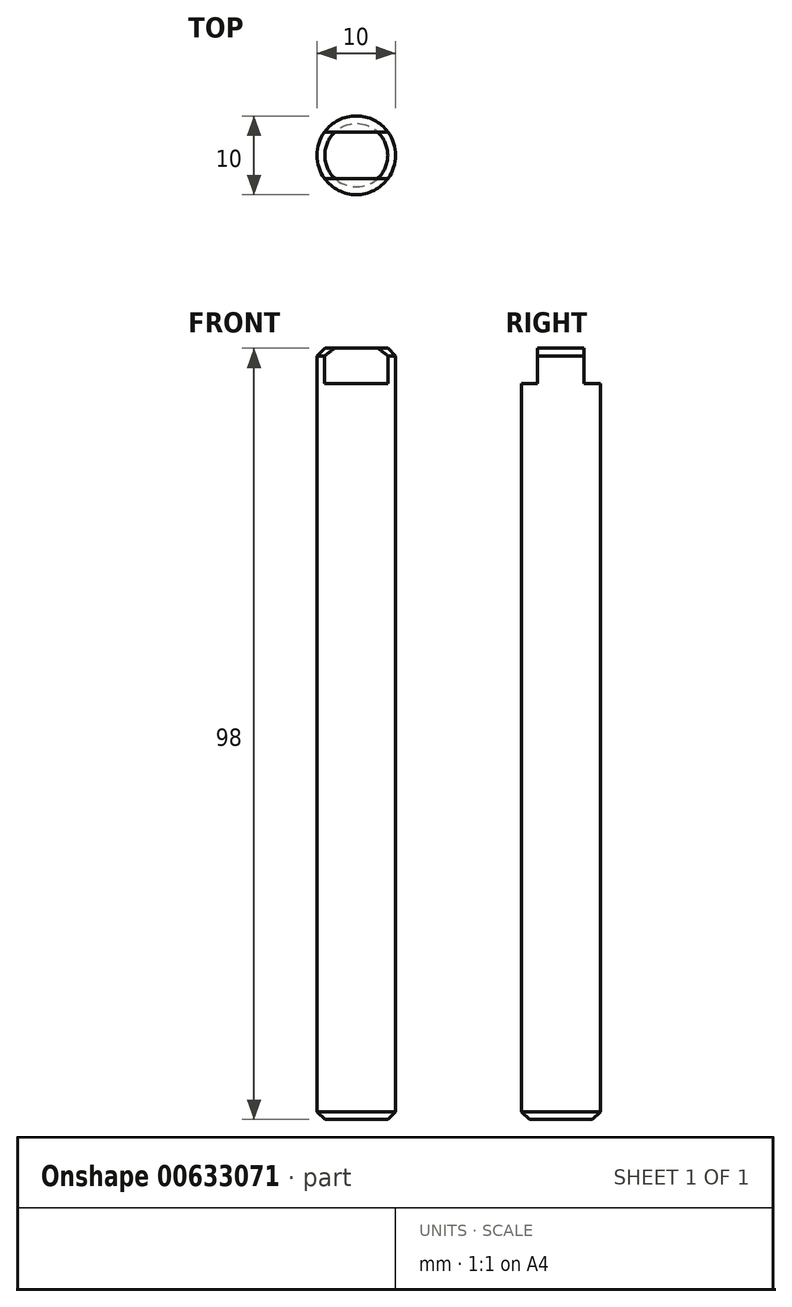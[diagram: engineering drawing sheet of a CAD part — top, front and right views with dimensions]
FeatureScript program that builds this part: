
annotation { "Feature Type Name" : "Feature", "Feature Type Description" : "" }
export const myFeature = defineFeature(function(context is Context, id is Id, definition is map)
    precondition{}
    {
        {
            var Q0;
            Q0=qCreatedBy(makeId("Top.planeOp"),FACE);
            var sketch = newSketch(context, id + "F0", { "sketchPlane" : qUnion([Q0])});
            skCircle(sketch, "E0", {"center": v(-1.1, 0) * mm, "radius": 5 * mm});
            skSolve(sketch);
        }
        {
            var Q0;
            Q0=makeQuery(id+"F0.imprint","IMPRINT",FACE,{"disambiguationData":[TD([[makeQuery(id+"F0.imprint","IMPRINT",EDGE,{"derivedFrom":sQuery(id+"F0.wireOp",EDGE,"E0")}),1.0]])]});
            extrude(context, id + "F1", {"entities" : qUnion([Q0]), "depth" : ((128.5 - 36.5) + 6) * mm, "offsetDistance" : 25 * mm});
        }
        {
            var Q0;
            Q0=qCreatedBy(makeId("Right.planeOp"),FACE);
            var sketch = newSketch(context, id + "F2", { "sketchPlane" : qUnion([Q0])});
            skLineSegment(sketch, "E1.bottom", {"start": v(2.95, 98) * mm, "end": v(7.82, 98) * mm});
            skLineSegment(sketch, "E1.top", {"start": v(2.95, 93.5) * mm, "end": v(7.82, 93.5) * mm});
            skLineSegment(sketch, "E1.left", {"start": v(2.95, 98) * mm, "end": v(2.95, 93.5) * mm});
            skLineSegment(sketch, "E1.right", {"start": v(7.82, 98) * mm, "end": v(7.82, 93.5) * mm});
            skLineSegment(sketch, "E2.bottom", {"start": v(-2.95, 98) * mm, "end": v(-8.14, 98) * mm});
            skLineSegment(sketch, "E2.top", {"start": v(-2.95, 93.5) * mm, "end": v(-8.14, 93.5) * mm});
            skLineSegment(sketch, "E2.left", {"start": v(-2.95, 98) * mm, "end": v(-2.95, 93.5) * mm});
            skLineSegment(sketch, "E2.right", {"start": v(-8.14, 98) * mm, "end": v(-8.14, 93.5) * mm});
            skSolve(sketch);
        }
        {
            var Q0;
            Q0 = qSketchRegion(id + "F2", true);
            extrude(context, id + "F3", {"entities" : qUnion([Q0]), "operationType" : NewBodyOperationType.REMOVE, "endBound" : BoundingType.SYMMETRIC, "oppositeDirection" : true, "depth" : 25 * mm, "offsetDistance" : 25 * mm});
        }
        {
            var Q0;
            Q0=makeQuery(id+"F3.boolean.opBoolean","SPLIT",EDGE,{"disambiguationData":[OD(1.0)],"derivedFrom":makeQuery(id+"F1.opExtrude","CAP_EDGE",EDGE,{"disambiguationData":[OSD([sQuery(id+"F0.wireOp",EDGE,"E0")])],"isStart":false})});
            var Q1;
            Q1=makeQuery(id+"F3.boolean.opBoolean","SPLIT",EDGE,{"disambiguationData":[OD(0.0)],"derivedFrom":makeQuery(id+"F1.opExtrude","CAP_EDGE",EDGE,{"disambiguationData":[OSD([sQuery(id+"F0.wireOp",EDGE,"E0")])],"isStart":false})});
            chamfer(context, id + "F4", {"entities" : qUnion([Q0, Q1]), "width" : 1 * mm, "tangentPropagation" : true});
        }
        {
            var Q0;
            Q0=makeQuery(id+"F1.opExtrude","CAP_EDGE",EDGE,{"disambiguationData":[OSD([sQuery(id+"F0.wireOp",EDGE,"E0")])],"isStart":true});
            chamfer(context, id + "F5", {"entities" : qUnion([Q0]), "width" : 1 * mm, "tangentPropagation" : true});
        }
    });
